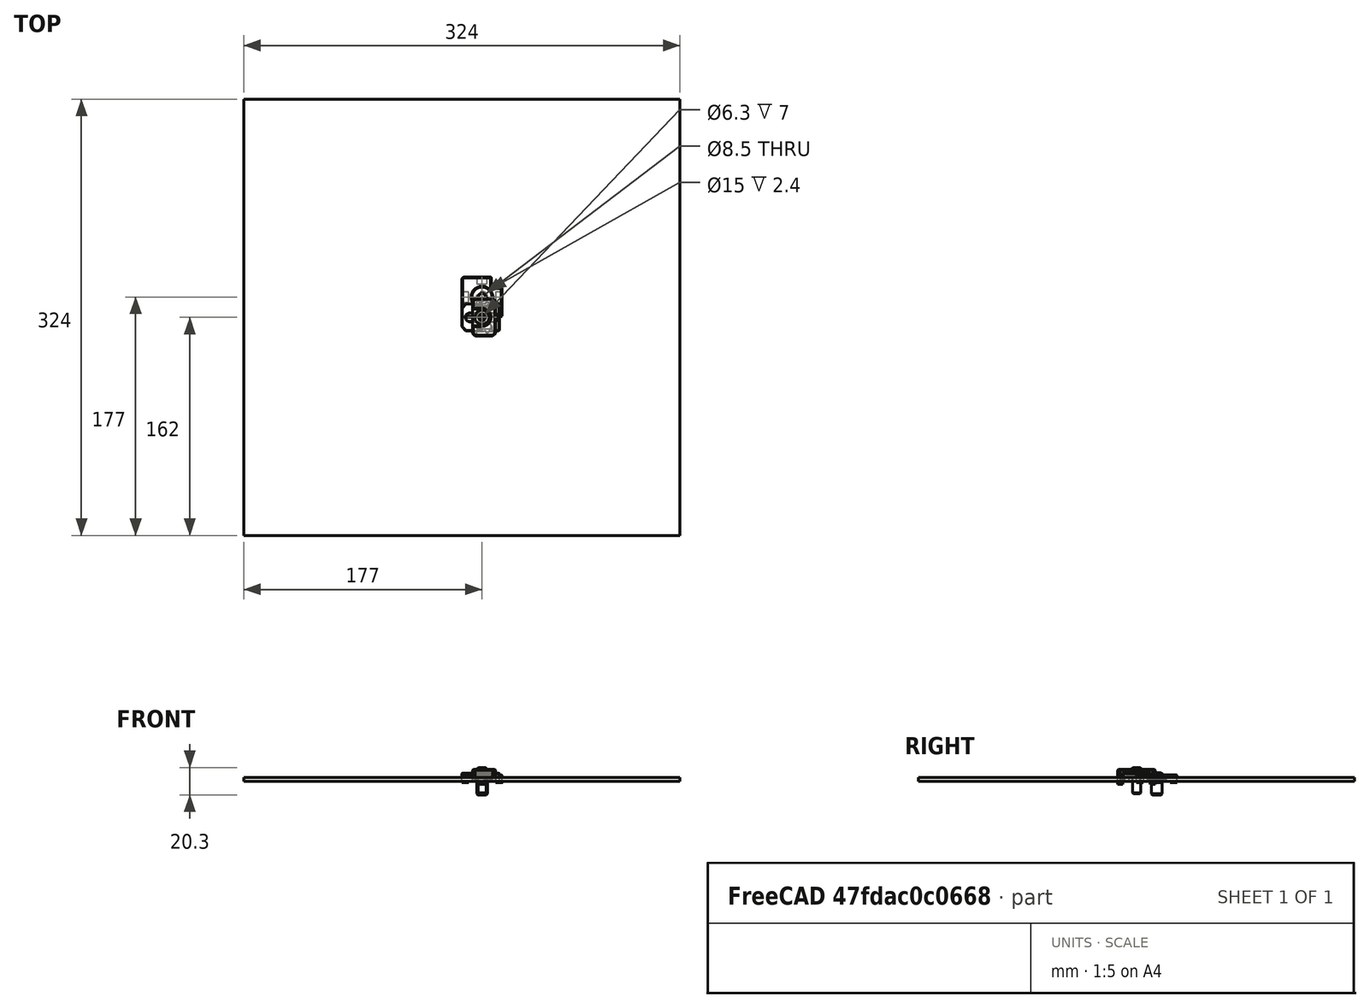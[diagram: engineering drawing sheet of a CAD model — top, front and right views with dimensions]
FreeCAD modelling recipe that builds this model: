
FCSTD DOCUMENT  (FreeCAD 0.19R24291 (Git))
Label: top-panel-assembly
License: All rights reserved
LicenseURL: http://en.wikipedia.org/wiki/All_rights_reserved
objects: Part::Feature×20, App::Part×13, Part::FeaturePython×12, Part::Box×1, PartDesign::CoordinateSystem×1
note: 34 computed .brp shape members not serialized (recipe doc carries the construction recipe); baked Part::Feature solids carry a one-line shape summary decoded from their .brp

FEATURE [Part::FeaturePython] Screw110  label="M8x12-Screw"  # Fasteners workbench fastener (typed FeaturePython)
  Placement = pos=(15,15,2) rot=(0,0,1;0rad)
  baseObject = -> Body001001 [Edge116]
  diameter = 5
  invert = false
  leftHanded = false
  length = 0
  lengthCustom = 12
  matchOuter = true
  offset = 0
  thread = false
  type = 40
FEATURE [Part::Feature] Chamfer008002001060  label="mounter-outer025"
  shape: bbox 17 x 28 x 11 mm, 53 faces (baked)
FEATURE [Part::FeaturePython] Screw084  label="M6x16-Screw034"  # Fasteners workbench fastener (typed FeaturePython)
  Placement = pos=(15,0,7) rot=(0,0,1;0rad)
  baseObject = -> Chamfer008002001049 [Edge135]
  diameter = 4
  invert = false
  leftHanded = false
  length = 3
  lengthCustom = 16
  matchOuter = false
  offset = 0
  thread = false
  type = 40
FEATURE [Part::Feature] Chamfer008002001052  label="mounter-inner027"
  shape: bbox 28 x 22 x 6 mm, 82 faces (baked)
FEATURE [Part::Feature] Chamfer008002001050  label="mounter-outer027"
  shape: bbox 17 x 28 x 11 mm, 53 faces (baked)
FEATURE [Part::Feature] Chamfer008002001056  label="mounter-outer021"
  shape: bbox 17 x 28 x 11 mm, 53 faces (baked)
FEATURE [Part::Feature] Body001002  label="corner-endcap001"
  Placement = pos=(0,0,0) rot=(0,1,0;3.14159rad)
  shape: bbox 30 x 30 x 6 mm, 52 faces (baked)
FEATURE [Part::FeaturePython] Screw082  label="M6x16-Screw032"  # Fasteners workbench fastener (typed FeaturePython)
  Placement = pos=(15,0,7) rot=(0,0,1;0rad)
  baseObject = -> Chamfer008002001057 [Edge135]
  diameter = 4
  invert = false
  leftHanded = false
  length = 3
  lengthCustom = 16
  matchOuter = false
  offset = 0
  thread = false
  type = 40
FEATURE [Part::Feature] Chamfer008002001051  label="mounter-inner021"
  shape: bbox 28 x 22 x 6 mm, 82 faces (baked)
FEATURE [Part::FeaturePython] Screw080  label="M6x16-Screw030"  # Fasteners workbench fastener (typed FeaturePython)
  Placement = pos=(15,0,7) rot=(0,0,1;0rad)
  baseObject = -> Chamfer008002001050 [Edge135]
  diameter = 4
  invert = false
  leftHanded = false
  length = 3
  lengthCustom = 16
  matchOuter = false
  offset = 0
  thread = false
  type = 40
FEATURE [Part::FeaturePython] Screw111  label="M8x12-Screw001"  # Fasteners workbench fastener (typed FeaturePython)
  Placement = pos=(15,15,2) rot=(0,0,1;0rad)
  baseObject = -> Body001002 [Edge116]
  diameter = 5
  invert = false
  leftHanded = false
  length = 0
  lengthCustom = 12
  matchOuter = true
  offset = 0
  thread = false
  type = 40
FEATURE [Part::FeaturePython] Screw083  label="M6x16-Screw033"  # Fasteners workbench fastener (typed FeaturePython)
  Placement = pos=(15,0,7) rot=(0,0,1;0rad)
  baseObject = -> Chamfer008002001056 [Edge135]
  diameter = 4
  invert = false
  leftHanded = false
  length = 3
  lengthCustom = 16
  matchOuter = false
  offset = 0
  thread = false
  type = 40
FEATURE [Part::FeaturePython] Screw112  label="M8x12-Screw002"  # Fasteners workbench fastener (typed FeaturePython)
  Placement = pos=(15,15,2) rot=(0,0,1;0rad)
  baseObject = -> Body001003 [Edge116]
  diameter = 5
  invert = false
  leftHanded = false
  length = 0
  lengthCustom = 12
  matchOuter = true
  offset = 0
  thread = false
  type = 40
FEATURE [Part::Feature] Chamfer008002001058  label="mounter-inner028"
  shape: bbox 28 x 22 x 6 mm, 82 faces (baked)
FEATURE [Part::Feature] Chamfer008002001049  label="mounter-outer023"
  shape: bbox 17 x 28 x 11 mm, 53 faces (baked)
FEATURE [Part::Feature] Body001003  label="corner-endcap002"
  Placement = pos=(0,0,0) rot=(0,1,0;3.14159rad)
  shape: bbox 30 x 30 x 6 mm, 52 faces (baked)
FEATURE [App::Part] Part055  label="endcap002"
  Group = -> [Body001003,Screw112]
  Origin = -> Origin055
  Placement = pos=(-185,-185,0) rot=(0,0,1;0rad)
FEATURE [Part::Feature] Chamfer008002001057  label="mounter-outer028"
  shape: bbox 17 x 28 x 11 mm, 53 faces (baked)
FEATURE [App::Part] Part045  label="Panel-mounterr2-030"
  Group = -> [Chamfer008002001051,Chamfer008002001057,Screw082]
  Origin = -> Origin041
  Placement = pos=(121,-155,0) rot=(0,0,-1;1.5708rad)
FEATURE [Part::Feature] Chamfer008002001055  label="mounter-outer022"
  shape: bbox 17 x 28 x 11 mm, 53 faces (baked)
FEATURE [Part::Feature] Body001001  label="corner-endcap"
  Placement = pos=(0,0,0) rot=(0,1,0;3.14159rad)
  shape: bbox 30 x 30 x 6 mm, 52 faces (baked)
FEATURE [Part::Feature] Chamfer008002001047  label="mounter-inner023"
  shape: bbox 28 x 22 x 6 mm, 82 faces (baked)
FEATURE [Part::Feature] Chamfer008002001059  label="mounter-outer026"
  shape: bbox 17 x 28 x 11 mm, 53 faces (baked)
FEATURE [App::Part] Part054  label="endcap001"
  Group = -> [Body001002,Screw111]
  Origin = -> Origin054
  Placement = pos=(185,-185,0) rot=(0,0,-1;4.71239rad)
FEATURE [Part::Feature] Chamfer008002001053  label="mounter-inner026"
  shape: bbox 28 x 22 x 6 mm, 82 faces (baked)
FEATURE [App::Part] Part040  label="Panel-mounterr2-026"
  Group = -> [Chamfer008002001053,Chamfer008002001049,Screw084]
  Origin = -> Origin037
  Placement = pos=(121,155,0) rot=(0,0,1;1.5708rad)
FEATURE [Part::FeaturePython] Screw113  label="M8x12-Screw003"  # Fasteners workbench fastener (typed FeaturePython)
  Placement = pos=(15,15,2) rot=(0,0,1;0rad)
  baseObject = -> Body001004 [Edge116]
  diameter = 5
  invert = false
  leftHanded = false
  length = 0
  lengthCustom = 12
  matchOuter = true
  offset = 0
  thread = false
  type = 40
FEATURE [Part::Feature] Chamfer008002001054  label="mounter-inner024"
  shape: bbox 28 x 22 x 6 mm, 82 faces (baked)
FEATURE [App::Part] Part053  label="endcap"
  Group = -> [Body001001,Screw110]
  Origin = -> Origin053
  Placement = pos=(185,185,0) rot=(0,0,1;3.14159rad)
FEATURE [Part::FeaturePython] Screw081  label="M6x16-Screw031"  # Fasteners workbench fastener (typed FeaturePython)
  Placement = pos=(15,0,7) rot=(0,0,1;0rad)
  baseObject = -> Chamfer008002001059 [Edge135]
  diameter = 4
  invert = false
  leftHanded = false
  length = 3
  lengthCustom = 16
  matchOuter = false
  offset = 0
  thread = false
  type = 40
FEATURE [App::Part] Part039  label="Panel-mounterr2-025"
  Group = -> [Chamfer008002001047,Chamfer008002001059,Screw081]
  Origin = -> Origin039
  Placement = pos=(-155,-96,0) rot=(0,0,-1;3.14159rad)
FEATURE [Part::Feature] Chamfer008002001061  label="mounter-inner025"
  shape: bbox 28 x 22 x 6 mm, 82 faces (baked)
FEATURE [Part::Feature] Chamfer008002001048  label="mounter-outer024"
  shape: bbox 17 x 28 x 11 mm, 53 faces (baked)
FEATURE [Part::Box] Box004  label="panel-324x234x3mm"
  AttacherType = Attacher::AttachEngine3D
  Height = 3
  Length = 324
  Placement = pos=(-162,-162,0) rot=(0,0,1;0rad)
  Width = 324
FEATURE [Part::Feature] Chamfer008002001046  label="mounter-inner022"
  shape: bbox 28 x 22 x 6 mm, 82 faces (baked)
FEATURE [App::Part] Part043  label="Panel-mounterr2-028"
  Group = -> [Chamfer008002001046,Chamfer008002001050,Screw080]
  Origin = -> Origin040
  Placement = pos=(-121,-155,0) rot=(0,0,-1;1.5708rad)
FEATURE [Part::FeaturePython] Screw078  label="M6x16-Screw028"  # Fasteners workbench fastener (typed FeaturePython)
  Placement = pos=(15,0,7) rot=(0,0,1;0rad)
  baseObject = -> Chamfer008002001055 [Edge135]
  diameter = 4
  invert = false
  leftHanded = false
  length = 3
  lengthCustom = 16
  matchOuter = false
  offset = 0
  thread = false
  type = 40
FEATURE [App::Part] Part041  label="Panel-mounterr2-027"
  Group = -> [Chamfer008002001052,Chamfer008002001055,Screw078]
  Origin = -> Origin038
  Placement = pos=(155,96,0) rot=(0,0,1;0rad)
FEATURE [Part::FeaturePython] Screw079  label="M6x16-Screw029"  # Fasteners workbench fastener (typed FeaturePython)
  Placement = pos=(15,0,7) rot=(0,0,1;0rad)
  baseObject = -> Chamfer008002001060 [Edge135]
  diameter = 4
  invert = false
  leftHanded = false
  length = 3
  lengthCustom = 16
  matchOuter = false
  offset = 0
  thread = false
  type = 40
FEATURE [App::Part] Part044  label="Panel-mounterr2-029"
  Group = -> [Chamfer008002001054,Chamfer008002001060,Screw079]
  Origin = -> Origin044
  Placement = pos=(-155,96,0) rot=(0,0,-1;3.14159rad)
FEATURE [Part::Feature] Body001004  label="corner-endcap003"
  Placement = pos=(0,0,0) rot=(0,1,0;3.14159rad)
  shape: bbox 30 x 30 x 6 mm, 52 faces (baked)
FEATURE [App::Part] Part056  label="endcap003"
  Group = -> [Body001004,Screw113]
  Origin = -> Origin056
  Placement = pos=(-185,185,0) rot=(0,0,1;4.71239rad)
FEATURE [PartDesign::CoordinateSystem] LCS_top_panel  label="LCS_top-panel"
  AttacherType = Attacher::AttachEngine3D
FEATURE [Part::FeaturePython] Screw077  label="M6x16-Screw027"  # Fasteners workbench fastener (typed FeaturePython)
  Placement = pos=(15,0,7) rot=(0,0,1;0rad)
  baseObject = -> Chamfer008002001048 [Edge135]
  diameter = 4
  invert = false
  leftHanded = false
  length = 3
  lengthCustom = 16
  matchOuter = false
  offset = 0
  thread = false
  type = 40
FEATURE [App::Part] Part038  label="Panel-mounterr2-024"
  Group = -> [Chamfer008002001061,Chamfer008002001048,Screw077]
  Origin = -> Origin045
  Placement = pos=(-121,155,0) rot=(0,0,1;1.5708rad)
FEATURE [App::Part] Part037  label="Panel-mounterr2-023"
  Group = -> [Chamfer008002001058,Chamfer008002001056,Screw083]
  Origin = -> Origin042
  Placement = pos=(155,-96,0) rot=(0,0,1;0rad)
FEATURE [App::Part] Part042  label="top-panel"
  Group = -> [Box004,Part037,Part041,Part040,Part038,Part044,Part039,Part043,Part045,LCS_top_panel,Part053,Part054,Part055,Part056]
  Origin = -> Origin043
